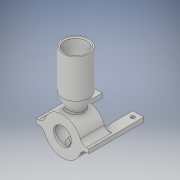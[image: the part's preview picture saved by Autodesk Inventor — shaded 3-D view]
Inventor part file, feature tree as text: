
AUTODESK INVENTOR PART (.ipt)
format: ipt  version: 2017 (Build 210142000, 142)  size: 317,440 bytes
history: native  units: in
note: dims shown in document units (in); Inventor stores cm internally (conversion verified against a paired STEP export)
features: sketch x8, extrude x5, fillet x5, plane x2, hole x2, revolve x1, chamfer x1, projected_geometry x1
ambient origin geometry x8: Origin, YZ Plane, XZ Plane, XY Plane, X Axis, Y Axis, Z Axis, Center Point
bodies: Solid1 (feature_tree)
feature tree (25):
  extrude  "Extrusion1"  Depth=0.25in
  extrude  "Extrusion2"  Depth=0.2in
  plane  "Work Plane1"
  hole  "Hole1"  [1 undecoded]
  plane  "Work Plane2"
  revolve  "Revolution1"  [1 undecoded]
  extrude  "Extrusion3"  TaperAngle=90.0deg  [1 undecoded]
  fillet  "Fillet1"  Radius=1.75in
  fillet  "Fillet2"  Radius=0.05in
  extrude  "Extrusion5"  Depth=0.05in
  chamfer  "Chamfer2"  Distance=1.0in
  extrude  "Extrusion6"  Depth=0.05in
  fillet  "Fillet3"  Radius=0.7in
  hole  "Hole2"  [1 undecoded]
  fillet  "Fillet4"  Radius=0.2in
  fillet  "Fillet5"  Radius=0.3in
  sketch  "Sketch1"  dims[d0=1.22in d1=0.25in]
  sketch  "Sketch2"  dims[d2=1.0in d3=0.0in d4=0.2in]
  sketch  "Sketch3"  dims[d5=0.1in d6=0.0in]
  sketch  "Sketch4"  dims[d7=0.35in d8=0.75in d9=0.375in d10=0.25in d11=0.5635in d12=0.5in d13=0.8108in d14=-0.5in]
  sketch  "Sketch5"  dims[d15=0.1in d16=1.5in]
  projected_geometry  "Projected Loop1"
  sketch  "Sketch7"  dims[d18=0.1in d19=90.0deg d20=1.75in d21=0.0in d22=0.05in]
  sketch  "Sketch8"  dims[d23=0.05in d30=0.05in d31=1.0in d32=0.0in]
  sketch  "Sketch9"  dims[d33=0.125in d34=0.125in d35=45.0deg d36=0.5in d37=0.7in d38=2.5in d39=0.2in d40=0.0in d41=0.3in d42=0.1667in d43=0.75in d44=0.375in d45=0.25in d46=0.5635in d47=0.5in d48=0.8108in d49=0.05in d50=0.05in d51=0.6in]
note: 4 required parameter values undecoded (feature->parameter linkage not recoverable at this tier; creation-order binding heuristic only, values carry confidence <= 0.55)